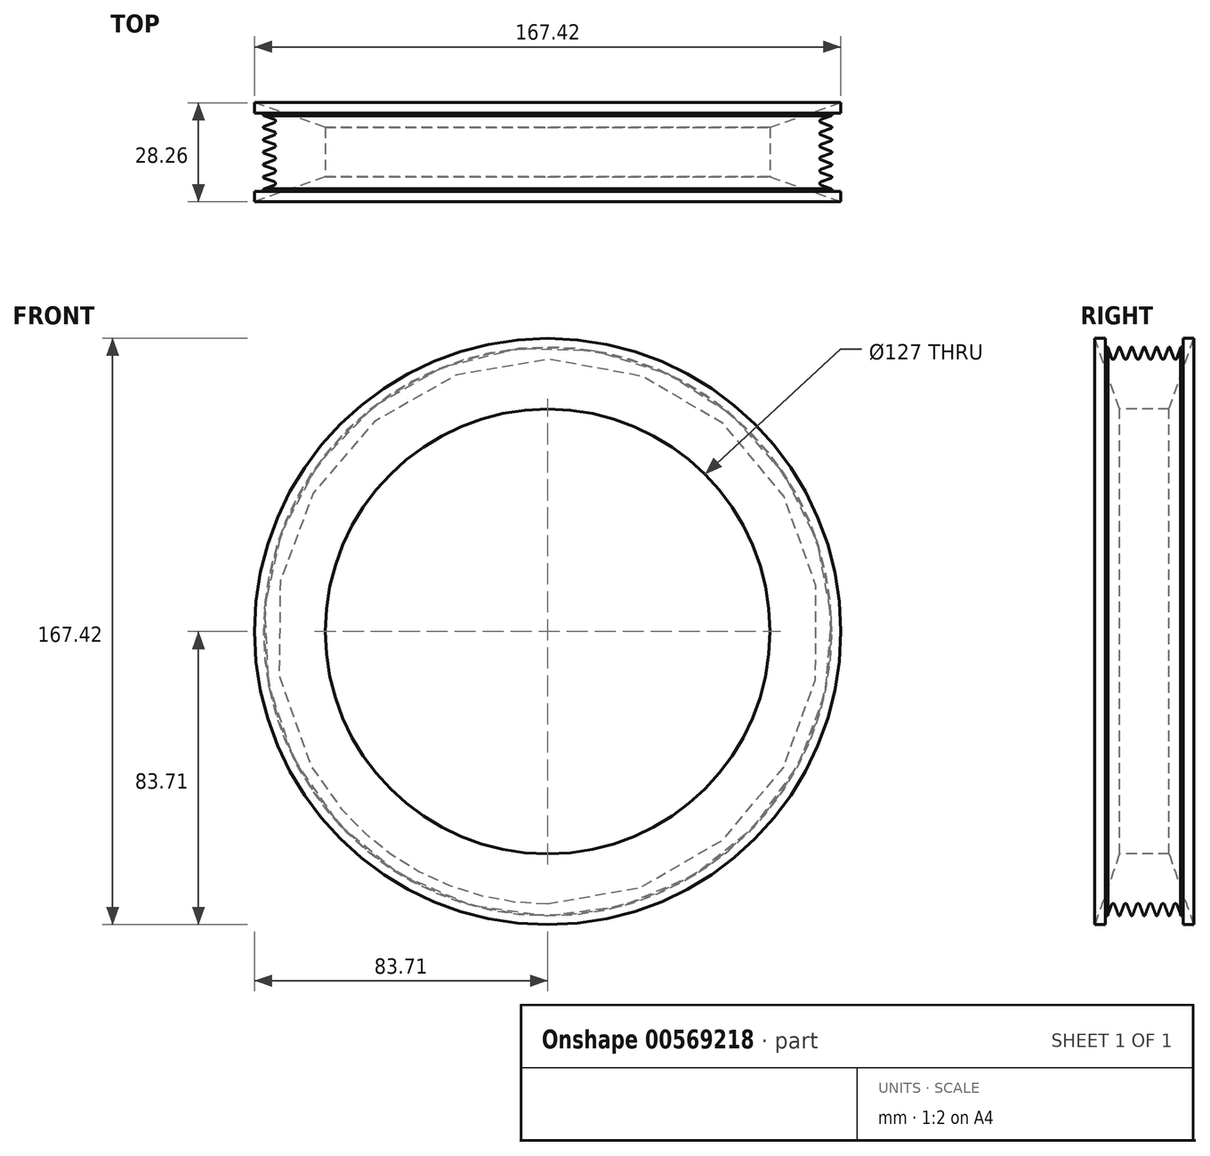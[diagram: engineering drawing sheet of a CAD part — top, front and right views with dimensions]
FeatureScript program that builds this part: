
annotation { "Feature Type Name" : "Feature", "Feature Type Description" : "" }
export const myFeature = defineFeature(function(context is Context, id is Id, definition is map)
    precondition{}
    {
        {
            var Q0;
            Q0=qCreatedBy(makeId("Right.planeOp"),FACE);
            var sketch = newSketch(context, id + "F0", { "sketchPlane" : qUnion([Q0])});
            skLineSegment(sketch, "E0", {"start": v(0, 0) * mm, "end": v(0, 63.5) * mm});
            skLineSegment(sketch, "E1", {"start": v(0, 63.5) * mm, "end": v(-7.06, 63.5) * mm});
            skLineSegment(sketch, "E2", {"start": v(-7.06, 63.5) * mm, "end": v(-12.4, 78.74) * mm});
            skLineSegment(sketch, "E3", {"start": v(-11.7, 76.75) * mm, "end": v(-13.41, 81.64) * mm});
            skLineSegment(sketch, "E4", {"start": v(-0.23, 81) * mm, "end": v(-1.31, 78.04) * mm});
            skLineSegment(sketch, "E5", {"start": v(-2.25, 78.04) * mm, "end": v(-3.33, 81) * mm});
            skLineSegment(sketch, "E6", {"start": v(-3.8, 81) * mm, "end": v(-4.87, 78.04) * mm});
            skLineSegment(sketch, "E7", {"start": v(-5.8, 78.04) * mm, "end": v(-6.89, 81) * mm});
            skLineSegment(sketch, "E8", {"start": v(-7.36, 81) * mm, "end": v(-8.43, 78.04) * mm});
            skLineSegment(sketch, "E9", {"start": v(-9.37, 78.04) * mm, "end": v(-10.41, 80.91) * mm});
            skPoint(sketch, "E10.end.orphan", {"position": v(-12.46, 81.64) * mm});
            skPoint(sketch, "E11.start.orphan", {"position": v(-10.68, 76.75) * mm});
            skPoint(sketch, "E12.orphan", {"position": v(-7.12, 76.75) * mm});
            skPoint(sketch, "E13.orphan", {"position": v(-1.78, 81.64) * mm});
            skPoint(sketch, "E14.start.orphan", {"position": v(-3.56, 76.75) * mm});
            skPoint(sketch, "E15.trimOffspring.end.orphan", {"position": v(-5.34, 81.64) * mm});
            skPoint(sketch, "E16.orphan", {"position": v(-8.9, 81.64) * mm});
            skPoint(sketch, "E17.visualSharp", {"position": v(-7.12, 81.64) * mm});
            skArc(sketch, "E17.filletArc", {"start": v(-6.89, 81) * mm, "mid": v(-7.12, 81.16) * mm, "end": v(-7.36, 81) * mm});
            skPoint(sketch, "E18.visualSharp", {"position": v(-3.56, 81.64) * mm});
            skArc(sketch, "E18.filletArc", {"start": v(-3.33, 81) * mm, "mid": v(-3.56, 81.16) * mm, "end": v(-3.8, 81) * mm});
            skPoint(sketch, "E19.visualSharp", {"position": v(-8.9, 76.75) * mm});
            skArc(sketch, "E19.filletArc", {"start": v(-9.37, 78.04) * mm, "mid": v(-8.9, 77.71) * mm, "end": v(-8.43, 78.04) * mm});
            skPoint(sketch, "E20.visualSharp", {"position": v(-5.34, 76.75) * mm});
            skArc(sketch, "E20.filletArc", {"start": v(-5.8, 78.04) * mm, "mid": v(-5.34, 77.71) * mm, "end": v(-4.87, 78.04) * mm});
            skPoint(sketch, "E21.visualSharp", {"position": v(-1.78, 76.75) * mm});
            skArc(sketch, "E21.filletArc", {"start": v(-2.25, 78.04) * mm, "mid": v(-1.78, 77.71) * mm, "end": v(-1.31, 78.04) * mm});
            skLineSegment(sketch, "E22", {"start": v(-7.12, 80.91) * mm, "end": v(-7.39, 80.91) * mm});
            skLineSegment(sketch, "E23", {"start": v(-10.41, 80.91) * mm, "end": v(-10.41, 81.17) * mm});
            skPoint(sketch, "E24.end.orphan", {"position": v(0, 76.75) * mm});
            skLineSegment(sketch, "E25", {"start": v(0, 76.75) * mm, "end": v(0, 63.5) * mm});
            skArc(sketch, "E26.MirrorCS", {"start": v(6.89, 81) * mm, "mid": v(7.12, 81.16) * mm, "end": v(7.36, 81) * mm});
            skLineSegment(sketch, "E27.MirrorCS", {"start": v(7.12, 80.91) * mm, "end": v(7.39, 80.91) * mm});
            skArc(sketch, "E28.MirrorCS", {"start": v(3.33, 81) * mm, "mid": v(3.56, 81.16) * mm, "end": v(3.8, 81) * mm});
            skArc(sketch, "E29.MirrorCS", {"start": v(5.8, 78.04) * mm, "mid": v(5.34, 77.71) * mm, "end": v(4.87, 78.04) * mm});
            skLineSegment(sketch, "E30.MirrorCS", {"start": v(10.41, 80.91) * mm, "end": v(10.41, 81.17) * mm});
            skArc(sketch, "E31.MirrorCS", {"start": v(9.37, 78.04) * mm, "mid": v(8.9, 77.71) * mm, "end": v(8.43, 78.04) * mm});
            skLineSegment(sketch, "E32.MirrorCS", {"start": v(3.8, 81) * mm, "end": v(4.87, 78.04) * mm});
            skLineSegment(sketch, "E33.MirrorCS", {"start": v(2.25, 78.04) * mm, "end": v(3.33, 81) * mm});
            skLineSegment(sketch, "E34.MirrorCS", {"start": v(9.37, 78.04) * mm, "end": v(10.41, 80.91) * mm});
            skLineSegment(sketch, "E35.MirrorCS", {"start": v(5.8, 78.04) * mm, "end": v(6.89, 81) * mm});
            skLineSegment(sketch, "E36.MirrorCS", {"start": v(7.36, 81) * mm, "end": v(8.43, 78.04) * mm});
            skArc(sketch, "E37.MirrorCS", {"start": v(2.25, 78.04) * mm, "mid": v(1.78, 77.71) * mm, "end": v(1.31, 78.04) * mm});
            skLineSegment(sketch, "E38.MirrorCS", {"start": v(11.7, 76.75) * mm, "end": v(13.41, 81.64) * mm});
            skLineSegment(sketch, "E39.MirrorCS", {"start": v(0.23, 81) * mm, "end": v(1.31, 78.04) * mm});
            skPoint(sketch, "E40.MirrorP", {"position": v(3.56, 81.64) * mm});
            skPoint(sketch, "E41.MirrorP", {"position": v(5.34, 76.75) * mm});
            skPoint(sketch, "E42.MirrorP", {"position": v(3.56, 76.75) * mm});
            skPoint(sketch, "E43.MirrorP", {"position": v(7.12, 76.75) * mm});
            skPoint(sketch, "E44.MirrorP", {"position": v(12.46, 81.64) * mm});
            skPoint(sketch, "E45.MirrorP", {"position": v(5.34, 81.64) * mm});
            skPoint(sketch, "E46.MirrorP", {"position": v(1.78, 76.75) * mm});
            skPoint(sketch, "E47.MirrorP", {"position": v(8.9, 76.75) * mm});
            skPoint(sketch, "E48.MirrorP", {"position": v(10.68, 76.75) * mm});
            skPoint(sketch, "E49.MirrorP", {"position": v(7.12, 81.64) * mm});
            skPoint(sketch, "E50.MirrorP", {"position": v(1.78, 81.64) * mm});
            skLineSegment(sketch, "E51.MirrorCS", {"start": v(7.06, 63.5) * mm, "end": v(12.4, 78.74) * mm});
            skLineSegment(sketch, "E52.MirrorCS", {"start": v(0, 63.5) * mm, "end": v(7.06, 63.5) * mm});
            skPoint(sketch, "E53.MirrorP", {"position": v(8.9, 81.64) * mm});
            skPoint(sketch, "E54.visualSharp", {"position": v(0, 81.64) * mm});
            skArc(sketch, "E54.filletArc", {"start": v(0.23, 81) * mm, "mid": v(0, 81.16) * mm, "end": v(-0.23, 81) * mm});
            skPoint(sketch, "E55.trimOffspring.start.orphan", {"position": v(-9.62, 78.74) * mm});
            skPoint(sketch, "E56.MirrorCS.start.orphan", {"position": v(9.62, 78.74) * mm});
            skLineSegment(sketch, "E57", {"start": v(0, 0) * mm, "end": v(28.34, 0) * mm});
            skLineSegment(sketch, "E58", {"start": v(-10.41, 81.17) * mm, "end": v(-11.15, 81.17) * mm});
            skLineSegment(sketch, "E59", {"start": v(-11.15, 81.17) * mm, "end": v(-11.15, 81.64) * mm});
            skPoint(sketch, "E60.start.orphan", {"position": v(-10.68, 81.64) * mm});
            skPoint(sketch, "E61.orphan", {"position": v(-10.41, 81.64) * mm});
            skLineSegment(sketch, "E62", {"start": v(10.41, 81.17) * mm, "end": v(10.41, 80.91) * mm});
            skLineSegment(sketch, "E63", {"start": v(10.41, 81.17) * mm, "end": v(11.15, 81.17) * mm});
            skLineSegment(sketch, "E64", {"start": v(11.15, 81.17) * mm, "end": v(11.15, 81.64) * mm});
            skPoint(sketch, "E65.MirrorCS.end.orphan", {"position": v(10.41, 81.64) * mm});
            skPoint(sketch, "E65.MirrorCS.start.orphan", {"position": v(10.68, 81.64) * mm});
            skLineSegment(sketch, "E66", {"start": v(11.15, 81.17) * mm, "end": v(11.15, 83.7) * mm});
            skPoint(sketch, "E66.endSnap0", {"position": v(11.15, 81.4) * mm});
            skLineSegment(sketch, "E67", {"start": v(11.15, 83.7) * mm, "end": v(14.13, 83.7) * mm});
            skLineSegment(sketch, "E68", {"start": v(7.06, 63.5) * mm, "end": v(14.13, 83.7) * mm});
            skLineSegment(sketch, "E69", {"start": v(-11.15, 81.17) * mm, "end": v(-11.15, 83.7) * mm});
            skLineSegment(sketch, "E70", {"start": v(-11.15, 83.7) * mm, "end": v(-14.13, 83.7) * mm});
            skLineSegment(sketch, "E71", {"start": v(-7.06, 63.5) * mm, "end": v(-14.13, 83.7) * mm});
            skSolve(sketch);
        }
        {
            var Q0;
            Q0=makeQuery(id+"F0.imprint","IMPRINT",FACE,{"disambiguationData":[TD([[makeQuery(id+"F0.imprint","IMPRINT",EDGE,{"derivedFrom":sQuery(id+"F0.wireOp",EDGE,"E1")}),-1.0]])]});
            var Q1;
            Q1=sQuery(id+"F0.wireOp",EDGE,"E57");
            revolve(context, id + "F1", {"entities" : qUnion([Q0]), "axis" : qUnion([Q1]), "revolveType" : RevolveType.FULL});
        }
    });
